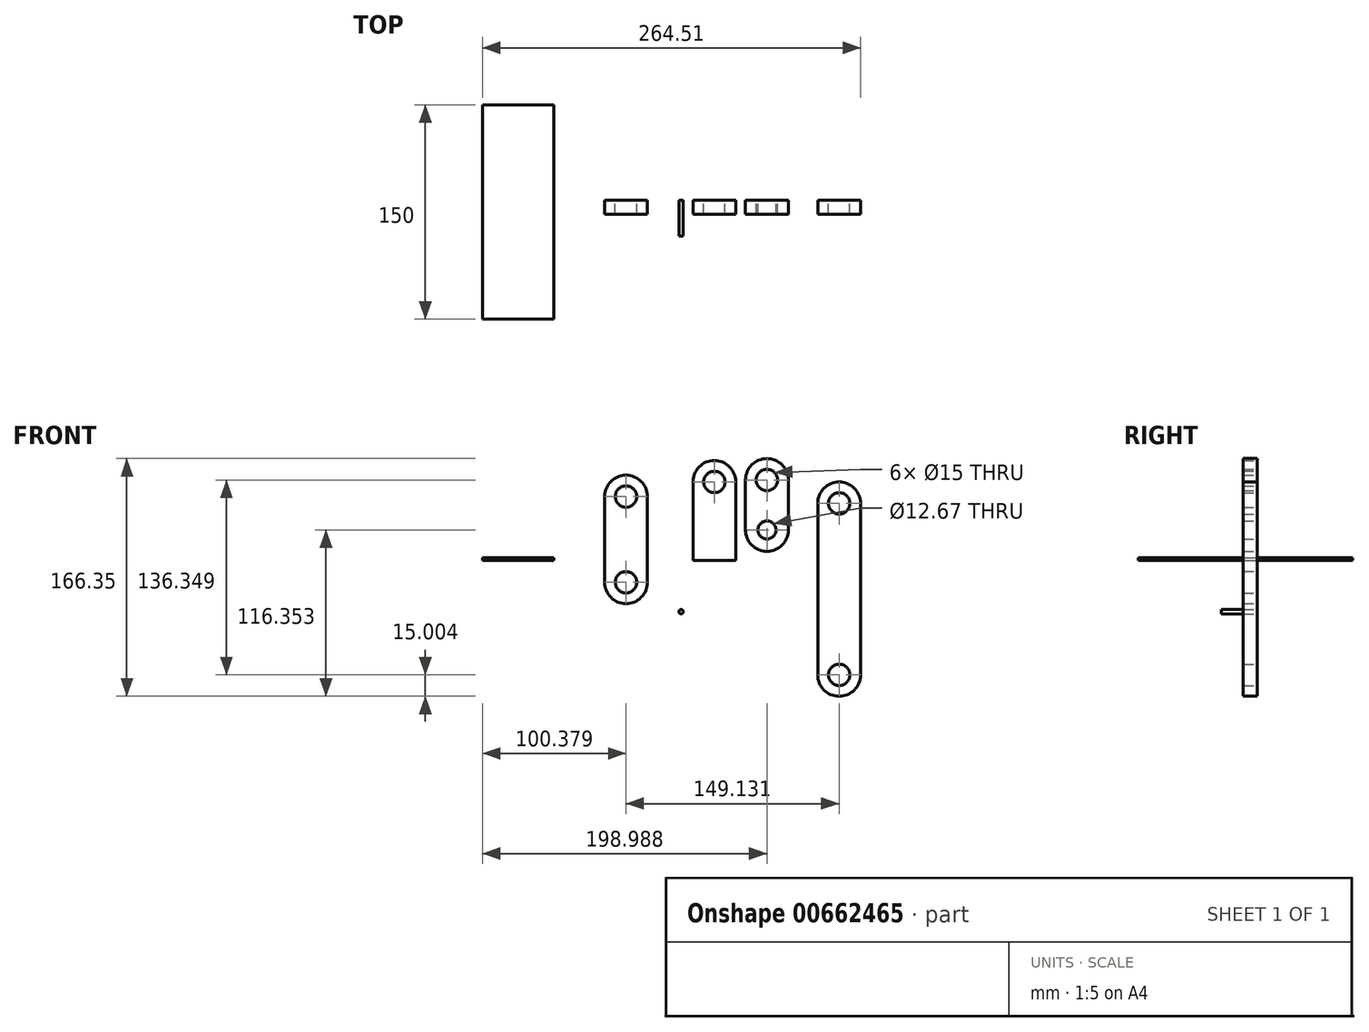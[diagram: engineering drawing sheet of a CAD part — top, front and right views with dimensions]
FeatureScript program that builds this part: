
annotation { "Feature Type Name" : "Feature", "Feature Type Description" : "" }
export const myFeature = defineFeature(function(context is Context, id is Id, definition is map)
    precondition{}
    {
        {
            var Q0;
            Q0=qCreatedBy(makeId("Front.planeOp"),FACE);
            var sketch = newSketch(context, id + "F0", { "sketchPlane" : qUnion([Q0])});
            skArc(sketch, "E0", {"start": v(15, 55) * mm, "mid": v(0, 70) * mm, "end": v(-15, 55) * mm});
            skLineSegment(sketch, "E1.top", {"start": v(-15, 0) * mm, "end": v(15, 0) * mm});
            skLineSegment(sketch, "E1.left", {"start": v(-15, 55) * mm, "end": v(-15, 0) * mm});
            skLineSegment(sketch, "E1.right", {"start": v(15, 55) * mm, "end": v(15, 0) * mm});
            skCircle(sketch, "E2", {"center": v(0, 55) * mm, "radius": 7.5 * mm});
            skSolve(sketch);
        }
        {
            var Q0;
            Q0 = qSketchRegion(id + "F0", true);
            extrude(context, id + "F1", {"entities" : qUnion([Q0]), "depth" : 10 * mm, "offsetDistance" : 25 * mm});
        }
        {
            var Q0;
            Q0=qCreatedBy(makeId("Front.planeOp"),FACE);
            var sketch = newSketch(context, id + "F2", { "sketchPlane" : qUnion([Q0])});
            skArc(sketch, "E3", {"start": v(-46.83, 44.81) * mm, "mid": v(-61.83, 59.81) * mm, "end": v(-76.83, 44.81) * mm});
            skArc(sketch, "E4", {"start": v(-76.83, -15.19) * mm, "mid": v(-61.83, -30.19) * mm, "end": v(-46.83, -15.19) * mm});
            skLineSegment(sketch, "E5", {"start": v(-76.83, 44.81) * mm, "end": v(-76.83, -15.19) * mm});
            skLineSegment(sketch, "E6", {"start": v(-46.83, 44.81) * mm, "end": v(-46.83, -15.19) * mm});
            skCircle(sketch, "E7", {"center": v(-61.83, 44.81) * mm, "radius": 7.5 * mm});
            skCircle(sketch, "E8", {"center": v(-61.83, -15.19) * mm, "radius": 7.5 * mm});
            skSolve(sketch);
        }
        {
            var Q0;
            Q0 = qSketchRegion(id + "F2", true);
            extrude(context, id + "F3", {"entities" : qUnion([Q0]), "depth" : 10 * mm, "offsetDistance" : 25 * mm});
        }
        {
            var Q0;
            Q0=qCreatedBy(makeId("Front.planeOp"),FACE);
            var sketch = newSketch(context, id + "F4", { "sketchPlane" : qUnion([Q0])});
            skArc(sketch, "E9", {"start": v(51.78, 56.37) * mm, "mid": v(36.78, 71.37) * mm, "end": v(21.78, 56.37) * mm});
            skArc(sketch, "E10", {"start": v(21.78, 21.37) * mm, "mid": v(36.78, 6.37) * mm, "end": v(51.78, 21.37) * mm});
            skLineSegment(sketch, "E11", {"start": v(21.78, 21.37) * mm, "end": v(21.78, 56.37) * mm});
            skLineSegment(sketch, "E12", {"start": v(51.78, 56.37) * mm, "end": v(51.78, 21.37) * mm});
            skCircle(sketch, "E13", {"center": v(36.78, 56.37) * mm, "radius": 7.5 * mm});
            skCircle(sketch, "E14", {"center": v(36.78, 21.37) * mm, "radius": 6.33 * mm});
            skSolve(sketch);
        }
        {
            var Q0;
            Q0 = qSketchRegion(id + "F4", true);
            extrude(context, id + "F5", {"entities" : qUnion([Q0]), "depth" : 10 * mm, "offsetDistance" : 25 * mm});
        }
        {
            var Q0;
            Q0=qCreatedBy(makeId("Front.planeOp"),FACE);
            var sketch = newSketch(context, id + "F6", { "sketchPlane" : qUnion([Q0])});
            skArc(sketch, "E15", {"start": v(102.3, 40.02) * mm, "mid": v(87.3, 55.02) * mm, "end": v(72.3, 40.02) * mm});
            skArc(sketch, "E16", {"start": v(72.3, -79.98) * mm, "mid": v(87.3, -94.98) * mm, "end": v(102.3, -79.98) * mm});
            skLineSegment(sketch, "E17", {"start": v(72.3, 40.02) * mm, "end": v(72.3, -79.98) * mm});
            skLineSegment(sketch, "E18", {"start": v(102.3, 40.02) * mm, "end": v(102.3, -79.98) * mm});
            skCircle(sketch, "E19", {"center": v(87.3, 40.02) * mm, "radius": 7.5 * mm});
            skCircle(sketch, "E20", {"center": v(87.3, -79.98) * mm, "radius": 7.5 * mm});
            skSolve(sketch);
        }
        {
            var Q0;
            Q0 = qSketchRegion(id + "F6", true);
            extrude(context, id + "F7", {"entities" : qUnion([Q0]), "depth" : 10 * mm, "offsetDistance" : 25 * mm});
        }
        {
            var Q0;
            Q0=qCreatedBy(makeId("Top.planeOp"),FACE);
            var sketch = newSketch(context, id + "F8", { "sketchPlane" : qUnion([Q0])});
            skLineSegment(sketch, "E21.bottom", {"start": v(-162.2, -83.31) * mm, "end": v(-112.2, -83.31) * mm});
            skLineSegment(sketch, "E21.top", {"start": v(-162.2, 66.69) * mm, "end": v(-112.2, 66.69) * mm});
            skLineSegment(sketch, "E21.left", {"start": v(-162.2, -83.31) * mm, "end": v(-162.2, 66.69) * mm});
            skLineSegment(sketch, "E21.right", {"start": v(-112.2, -83.31) * mm, "end": v(-112.2, 66.69) * mm});
            skSolve(sketch);
        }
        {
            var Q0;
            Q0 = qSketchRegion(id + "F8", true);
            extrude(context, id + "F9", {"entities" : qUnion([Q0]), "depth" : 2 * mm, "offsetDistance" : 25 * mm});
        }
        {
            var Q0;
            Q0=qCreatedBy(makeId("Front.planeOp"),FACE);
            var sketch = newSketch(context, id + "F10", { "sketchPlane" : qUnion([Q0])});
            skCircle(sketch, "E22", {"center": v(-23.27, -35.78) * mm, "radius": 1.5 * mm});
            skSolve(sketch);
        }
        {
            var Q0;
            Q0 = qSketchRegion(id + "F10", true);
            extrude(context, id + "F11", {"entities" : qUnion([Q0]), "depth" : 25 * mm, "offsetDistance" : 25 * mm});
        }
    });
